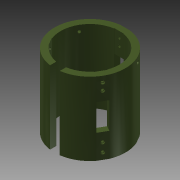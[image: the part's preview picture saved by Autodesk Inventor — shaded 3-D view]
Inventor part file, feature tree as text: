
AUTODESK INVENTOR PART (.ipt)
format: ipt  version: 2013 (Build 170138000, 138)  size: 444,928 bytes
history: native  units: mm
features: sketch x21, extrude x15, other x6, pattern_circular x5, hole x4
ambient origin geometry x8: Origin, YZ Plane, XZ Plane, XY Plane, X Axis, Y Axis, Z Axis, Center Point
feature tree (51):
  other  "ソリッド1"
  extrude  "押し出し1"  Depth=26.0mm
  extrude  "押し出し2"  Depth=20.0mm
  hole  "穴1"  [1 undecoded]
  pattern_circular  "円形状パターン1"  [2 undecoded]
  sketch  "スケッチ4"
  other  "作業平面1"
  other  "作業平面3"
  other  "作業平面7"
  extrude  "押し出し3"  Depth=10.8mm
  pattern_circular  "円形状パターン2"  [2 undecoded]
  other  "作業平面8"
  hole  "穴2"  [1 undecoded]
  pattern_circular  "円形状パターン3"  Count=3 Angle=360.0deg
  extrude  "押し出し4"  Depth=19.5mm
  extrude  "押し出し5"  Depth=4.7mm
  extrude  "押し出し6"  Depth=50.6mm
  extrude  "押し出し7"  Depth=3.0mm
  sketch  "スケッチ11"
  other  "作業平面9"
  extrude  "押し出し8"  Depth=3.0mm
  extrude  "押し出し9"  Depth=5.1mm
  extrude  "押し出し10"  Depth=4.7mm
  extrude  "押し出し11"  Depth=3.0mm
  extrude  "押し出し12"  Depth=50.6mm
  hole  "穴3"  [1 undecoded]
  extrude  "押し出し13"  Depth=30.0mm TaperAngle=360.0deg
  extrude  "押し出し14"  Depth=60.0mm TaperAngle=360.0deg
  extrude  "押し出し15"  Depth=24.2mm
  hole  "穴4"  [1 undecoded]
  pattern_circular  "円形状パターン4"  [2 undecoded]
  pattern_circular  "円形状パターン5"  [2 undecoded]
  sketch  "スケッチ1"
  sketch  "スケッチ2"
  sketch  "スケッチ3"
  sketch  "スケッチ5"
  sketch  "スケッチ6"
  sketch  "スケッチ7"
  sketch  "スケッチ8"
  sketch  "スケッチ9"
  sketch  "スケッチ10"
  sketch  "スケッチ12"
  sketch  "スケッチ13"
  sketch  "スケッチ14"
  sketch  "スケッチ15"
  sketch  "スケッチ16"
  sketch  "スケッチ17"
  sketch  "スケッチ18"
  sketch  "スケッチ19"
  sketch  "スケッチ20"
  sketch  "スケッチ21"
note: 12 required parameter values undecoded (feature->parameter linkage not recoverable at this tier; creation-order binding heuristic only, values carry confidence <= 0.55)
